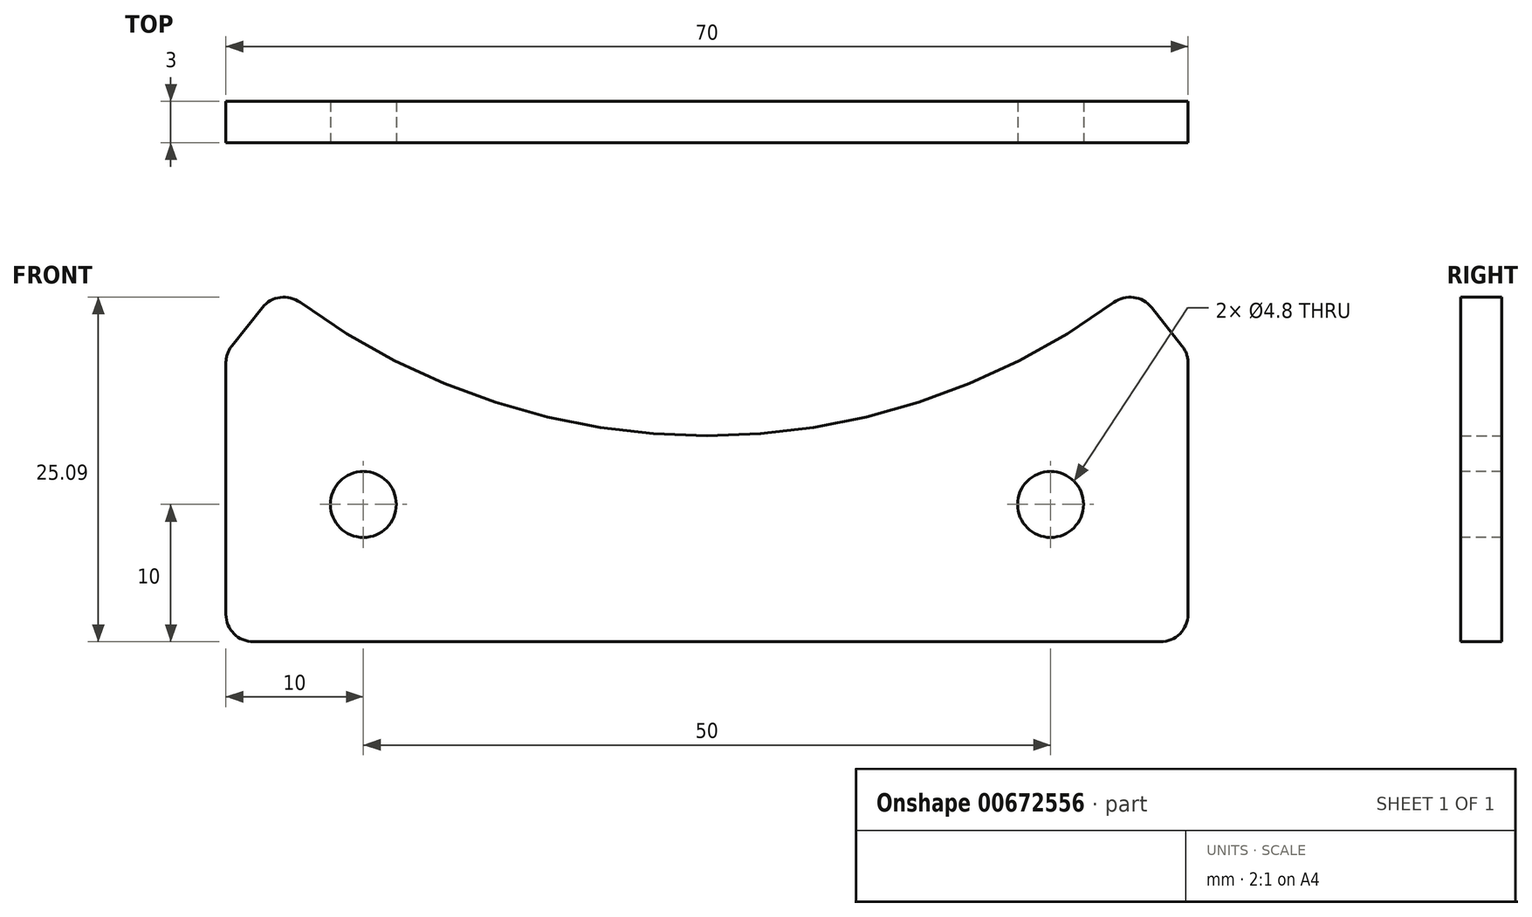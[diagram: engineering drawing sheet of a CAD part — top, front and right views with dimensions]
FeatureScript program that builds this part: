
annotation { "Feature Type Name" : "Feature", "Feature Type Description" : "" }
export const myFeature = defineFeature(function(context is Context, id is Id, definition is map)
    precondition{}
    {
        {
            var Q0;
            Q0=qCreatedBy(makeId("Front.planeOp"),FACE);
            var sketch = newSketch(context, id + "F0", { "sketchPlane" : qUnion([Q0])});
            skArc(sketch, "E0", {"start": v(-31.13, -39.13) * mm, "mid": v(0, -50) * mm, "end": v(31.13, -39.13) * mm});
            skLineSegment(sketch, "E1", {"start": v(31.13, -39.13) * mm, "end": v(35, -44) * mm});
            skLineSegment(sketch, "E2", {"start": v(-31.13, -39.13) * mm, "end": v(-35, -44) * mm});
            skLineSegment(sketch, "E3", {"start": v(0, 0) * mm, "end": v(0, -50) * mm});
            skLineSegment(sketch, "E4", {"start": v(-35, -44) * mm, "end": v(-35, -65) * mm});
            skLineSegment(sketch, "E5", {"start": v(35, -44) * mm, "end": v(35, -65) * mm});
            skLineSegment(sketch, "E6", {"start": v(-35, -65) * mm, "end": v(35, -65) * mm});
            skSolve(sketch);
        }
        {
            var Q0;
            {var subQ1=sQuery(id+"F0.wireOp",EDGE,"E1");Q0=makeQuery(id+"F0.imprint","IMPRINT",FACE,{"disambiguationData":[TD([[makeQuery(id+"F0.imprint","IMPRINT",EDGE,{"derivedFrom":subQ1}),-1.0]])]});}
            extrude(context, id + "F1", {"entities" : qUnion([Q0]), "endBound" : BoundingType.SYMMETRIC, "depth" : 3 * mm, "offsetDistance" : 25 * mm});
        }
        {
            var Q0;
            Q0=makeQuery(id+"F1.opExtrude","SWEPT_EDGE",EDGE,{"disambiguationData":[OSD([sQuery(id+"F0.wireOp",EDGE,"E0"),sQuery(id+"F0.wireOp",EDGE,"E1")])]});
            var Q1;
            Q1=makeQuery(id+"F1.opExtrude","SWEPT_EDGE",EDGE,{"disambiguationData":[OSD([sQuery(id+"F0.wireOp",EDGE,"E1"),sQuery(id+"F0.wireOp",EDGE,"E5")])]});
            var Q2;
            Q2=makeQuery(id+"F1.opExtrude","SWEPT_EDGE",EDGE,{"disambiguationData":[OSD([sQuery(id+"F0.wireOp",EDGE,"E5"),sQuery(id+"F0.wireOp",EDGE,"E6")])]});
            var Q3;
            Q3=makeQuery(id+"F1.opExtrude","SWEPT_EDGE",EDGE,{"disambiguationData":[OSD([sQuery(id+"F0.wireOp",EDGE,"E0"),sQuery(id+"F0.wireOp",EDGE,"E2")])]});
            var Q4;
            Q4=makeQuery(id+"F1.opExtrude","SWEPT_EDGE",EDGE,{"disambiguationData":[OSD([sQuery(id+"F0.wireOp",EDGE,"E2"),sQuery(id+"F0.wireOp",EDGE,"E4")])]});
            var Q5;
            Q5=makeQuery(id+"F1.opExtrude","SWEPT_EDGE",EDGE,{"disambiguationData":[OSD([sQuery(id+"F0.wireOp",EDGE,"E4"),sQuery(id+"F0.wireOp",EDGE,"E6")])]});
            fillet(context, id + "F2", {"entities" : qUnion([Q0, Q1, Q2, Q3, Q4, Q5]), "radius" : 2 * mm, "tangentPropagation" : true, "allowEdgeOverflow" : false});
        }
        {
            var Q0;
            Q0=makeQuery(id+"F1.opExtrude","CAP_FACE",FACE,{"disambiguationData":[OSD([sQuery(id+"F0.wireOp",EDGE,"E0"),sQuery(id+"F0.wireOp",EDGE,"E1"),sQuery(id+"F0.wireOp",EDGE,"E2"),sQuery(id+"F0.wireOp",EDGE,"E4"),sQuery(id+"F0.wireOp",EDGE,"E5"),sQuery(id+"F0.wireOp",EDGE,"E6")])],"isStart":false});
            var sketch = newSketch(context, id + "F3", { "sketchPlane" : qUnion([Q0])});
            skCircle(sketch, "E7", {"center": v(-25, -55) * mm, "radius": 2.4 * mm});
            skCircle(sketch, "E8", {"center": v(25, -55) * mm, "radius": 2.4 * mm});
            skSolve(sketch);
        }
        {
            var Q0;
            Q0=makeQuery(id+"F3.imprint","IMPRINT",FACE,{"disambiguationData":[TD([[makeQuery(id+"F3.imprint","IMPRINT",EDGE,{"derivedFrom":sQuery(id+"F3.wireOp",EDGE,"E7")}),1.0]])]});
            var Q1;
            Q1=makeQuery(id+"F3.imprint","IMPRINT",FACE,{"disambiguationData":[TD([[makeQuery(id+"F3.imprint","IMPRINT",EDGE,{"derivedFrom":sQuery(id+"F3.wireOp",EDGE,"E8")}),1.0]])]});
            extrude(context, id + "F4", {"entities" : qUnion([Q0, Q1]), "operationType" : NewBodyOperationType.REMOVE, "oppositeDirection" : true, "depth" : 25 * mm, "offsetDistance" : 25 * mm});
        }
    });
